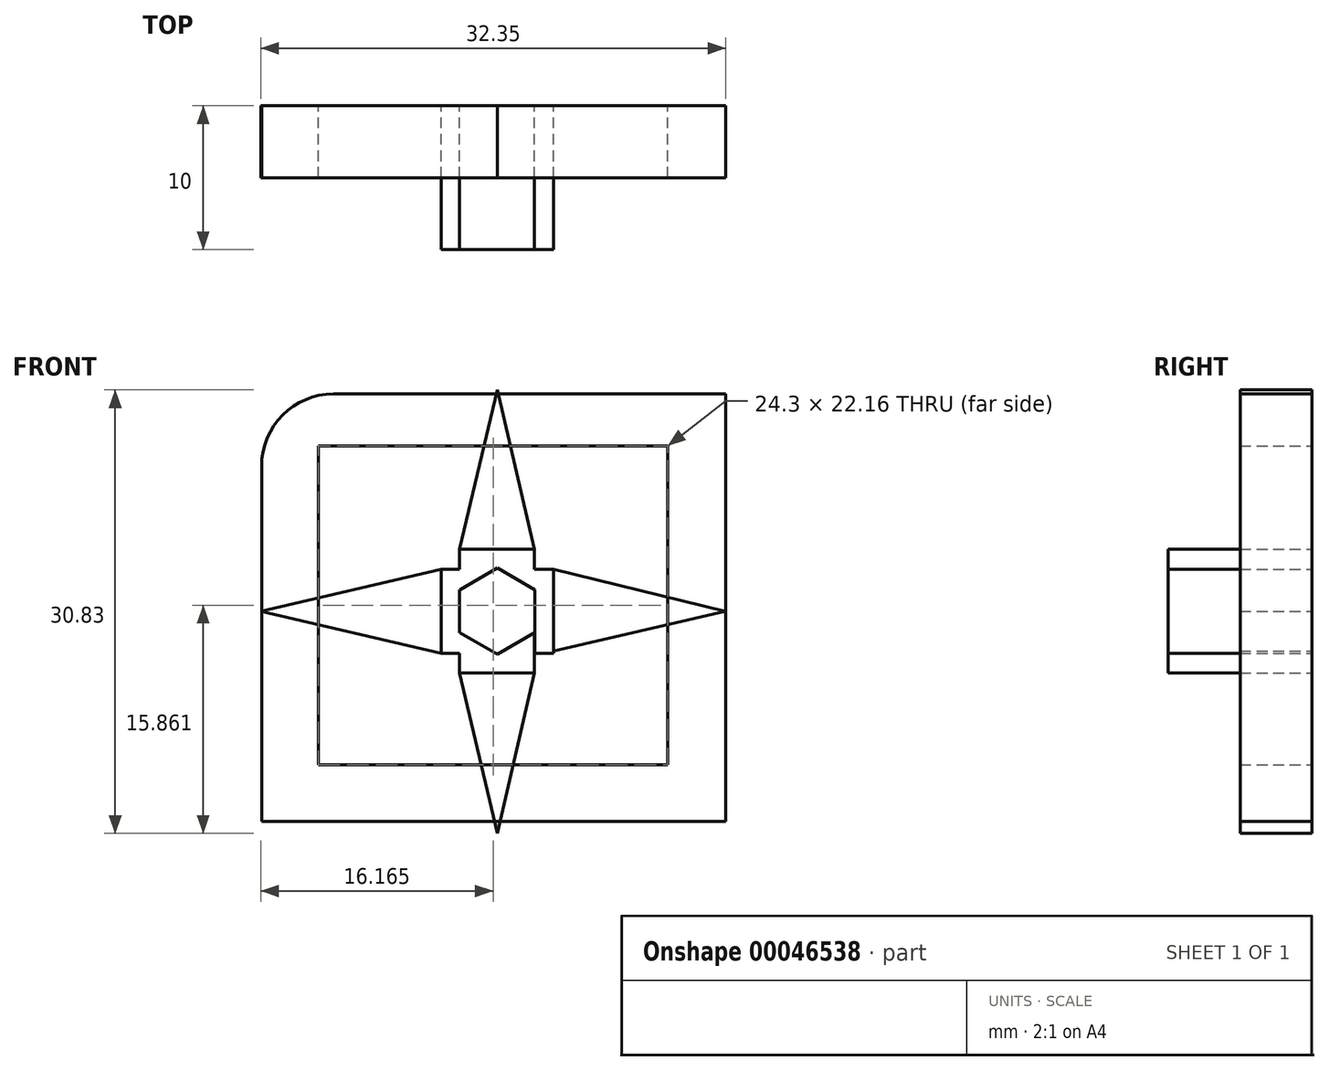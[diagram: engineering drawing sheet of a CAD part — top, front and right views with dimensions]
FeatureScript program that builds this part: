
annotation { "Feature Type Name" : "Feature", "Feature Type Description" : "" }
export const myFeature = defineFeature(function(context is Context, id is Id, definition is map)
    precondition{}
    {
        {
            var Q0;
            Q0=qCreatedBy(makeId("Front.planeOp"),FACE);
            var sketch = newSketch(context, id + "F0", { "sketchPlane" : qUnion([Q0])});
            skCircle(sketch, "E0.cCircle", {"center": v(0, 0) * mm, "radius": 2.6 * mm, "construction": true});
            skLineSegment(sketch, "E0.0", {"start": v(-2.6, -1.5) * mm, "end": v(-2.6, 1.5) * mm});
            skLineSegment(sketch, "E0.1", {"start": v(-2.6, 1.5) * mm, "end": v(0, 3) * mm});
            skLineSegment(sketch, "E0.2", {"start": v(0, 3) * mm, "end": v(2.6, 1.5) * mm});
            skLineSegment(sketch, "E0.3", {"start": v(2.6, 1.5) * mm, "end": v(2.6, -1.5) * mm});
            skLineSegment(sketch, "E0.4", {"start": v(2.6, -1.5) * mm, "end": v(0, -3) * mm});
            skLineSegment(sketch, "E0.5", {"start": v(0, -3) * mm, "end": v(-2.6, -1.5) * mm});
            skPoint(sketch, "E0.0.midPoint", {"position": v(-2.6, 0) * mm});
            skSolve(sketch);
        }
        {
            var Q0;
            Q0=makeQuery(id+"F0.imprint","IMPRINT",FACE,{"disambiguationData":[TD([[makeQuery(id+"F0.imprint","IMPRINT",EDGE,{"derivedFrom":sQuery(id+"F0.wireOp",EDGE,"E0.0")}),-1.0]])]});
            var sketch = newSketch(context, id + "F1", { "sketchPlane" : qUnion([Q0])});
            skLineSegment(sketch, "E1.bottom", {"start": v(-2.63, 1.5) * mm, "end": v(2.6, 1.5) * mm});
            skLineSegment(sketch, "E1.top", {"start": v(-2.63, 2.93) * mm, "end": v(2.6, 2.93) * mm});
            skLineSegment(sketch, "E1.left", {"start": v(-2.63, 1.5) * mm, "end": v(-2.63, 2.93) * mm});
            skLineSegment(sketch, "E1.right", {"start": v(2.6, 1.5) * mm, "end": v(2.6, 2.93) * mm});
            skLineSegment(sketch, "E2.bottom", {"start": v(-2.63, -1.48) * mm, "end": v(2.58, -1.48) * mm});
            skLineSegment(sketch, "E2.top", {"start": v(-2.63, -2.92) * mm, "end": v(2.58, -2.92) * mm});
            skLineSegment(sketch, "E2.left", {"start": v(-2.63, -1.48) * mm, "end": v(-2.63, -2.92) * mm});
            skLineSegment(sketch, "E2.right", {"start": v(2.58, -1.48) * mm, "end": v(2.58, -2.92) * mm});
            skLineSegment(sketch, "E3.bottom", {"start": v(-2.63, 2.93) * mm, "end": v(-3.9, 2.93) * mm});
            skLineSegment(sketch, "E3.top", {"start": v(-2.63, -2.92) * mm, "end": v(-3.9, -2.92) * mm});
            skLineSegment(sketch, "E3.left", {"start": v(-2.63, 2.93) * mm, "end": v(-2.63, -2.92) * mm});
            skLineSegment(sketch, "E3.right", {"start": v(-3.9, 2.93) * mm, "end": v(-3.9, -2.92) * mm});
            skLineSegment(sketch, "E4.bottom", {"start": v(2.6, 2.93) * mm, "end": v(3.9, 2.93) * mm});
            skLineSegment(sketch, "E4.top", {"start": v(2.6, -2.92) * mm, "end": v(3.9, -2.92) * mm});
            skLineSegment(sketch, "E4.left", {"start": v(2.6, 2.93) * mm, "end": v(2.6, -2.92) * mm});
            skLineSegment(sketch, "E4.right", {"start": v(3.9, 2.93) * mm, "end": v(3.9, -2.92) * mm});
            skLineSegment(sketch, "E5.bottom", {"start": v(-2.63, 2.93) * mm, "end": v(2.58, 2.93) * mm});
            skLineSegment(sketch, "E5.top", {"start": v(-2.63, 4.32) * mm, "end": v(2.58, 4.32) * mm});
            skLineSegment(sketch, "E5.left", {"start": v(-2.63, 2.93) * mm, "end": v(-2.63, 4.32) * mm});
            skLineSegment(sketch, "E5.right", {"start": v(2.58, 2.93) * mm, "end": v(2.58, 4.32) * mm});
            skLineSegment(sketch, "E6.top", {"start": v(-2.63, -4.28) * mm, "end": v(2.58, -4.28) * mm});
            skLineSegment(sketch, "E6.left", {"start": v(-2.63, -2.92) * mm, "end": v(-2.63, -4.28) * mm});
            skLineSegment(sketch, "E6.right", {"start": v(2.58, -2.92) * mm, "end": v(2.58, -4.28) * mm});
            skSolve(sketch);
        }
        {
            var Q0;
            {var subQ1=makeQuery(id+"F0.imprint","IMPRINT",EDGE,{"derivedFrom":sQuery(id+"F0.wireOp",EDGE,"E0.4")});var subQ3=sQuery(id+"F1.wireOp",EDGE,"E2.right");var subQ5=makeQuery(id+"F1.imprint","INTERSECT",VERTEX,{"derivedFrom":[subQ1,subQ3]});Q0=makeQuery(id+"F1.imprint","IMPRINT",FACE,{"disambiguationData":[TD([[makeQuery(id+"F1.imprint","IMPRINT",EDGE,{"disambiguationData":[TD([[subQ5,-1.0]])],"derivedFrom":subQ1}),1.0]])]});}
            var Q1;
            {var subQ0=sQuery(id+"F1.wireOp",EDGE,"E4.bottom");Q1=makeQuery(id+"F1.imprint","IMPRINT",FACE,{"disambiguationData":[TD([[makeQuery(id+"F1.imprint","IMPRINT",EDGE,{"derivedFrom":subQ0}),-1.0]])]});}
            var Q2;
            {var subQ9=sQuery(id+"F1.wireOp",EDGE,"E1.top");Q2=makeQuery(id+"F1.imprint","IMPRINT",FACE,{"disambiguationData":[TD([[makeQuery(id+"F1.imprint","IMPRINT",EDGE,{"derivedFrom":subQ9}),-1.0]])]});}
            var Q3;
            Q3=makeQuery(id+"F1.imprint","IMPRINT",FACE,{"disambiguationData":[TD([[makeQuery(id+"F1.imprint","IMPRINT",EDGE,{"derivedFrom":sQuery(id+"F1.wireOp",EDGE,"E5.top")}),-1.0]])]});
            var Q4;
            {var subQ5=sQuery(id+"F1.wireOp",EDGE,"E1.bottom");var subQ7=sQuery(id+"F1.wireOp",EDGE,"E3.left");var subQ8=makeQuery(id+"F1.imprint","INTERSECT",VERTEX,{"derivedFrom":[subQ5,subQ7]});Q4=makeQuery(id+"F1.imprint","IMPRINT",FACE,{"disambiguationData":[TD([[makeQuery(id+"F1.imprint","IMPRINT",EDGE,{"disambiguationData":[TD([[subQ8,-1.0]])],"derivedFrom":subQ5}),1.0]])]});}
            var Q5;
            {var subQ3=sQuery(id+"F1.wireOp",EDGE,"E3.bottom");Q5=makeQuery(id+"F1.imprint","IMPRINT",FACE,{"disambiguationData":[TD([[makeQuery(id+"F1.imprint","IMPRINT",EDGE,{"derivedFrom":subQ3}),1.0]])]});}
            var Q6;
            Q6=makeQuery(id+"F1.imprint","IMPRINT",FACE,{"disambiguationData":[TD([[makeQuery(id+"F1.imprint","IMPRINT",EDGE,{"derivedFrom":sQuery(id+"F1.wireOp",EDGE,"E6.top")}),1.0]])]});
            var Q7;
            {var subQ0=sQuery(id+"F1.wireOp",EDGE,"E2.bottom");var subQ3=sQuery(id+"F1.wireOp",EDGE,"E3.left");var subQ4=makeQuery(id+"F1.imprint","INTERSECT",VERTEX,{"derivedFrom":[subQ0,subQ3]});Q7=makeQuery(id+"F1.imprint","IMPRINT",FACE,{"disambiguationData":[TD([[makeQuery(id+"F1.imprint","IMPRINT",EDGE,{"disambiguationData":[TD([[subQ4,-1.0]])],"derivedFrom":subQ0}),-1.0]])]});}
            extrude(context, id + "F2", {"entities" : qUnion([Q0, Q1, Q2, Q3, Q4, Q5, Q6, Q7]), "depth" : 10 * mm});
        }
        {
            var Q0;
            Q0=makeQuery(id+"F2.opExtrude","CAP_FACE",FACE,{"disambiguationData":[OSD([sQuery(id+"F0.wireOp",EDGE,"E0.0"),sQuery(id+"F0.wireOp",EDGE,"E0.1"),sQuery(id+"F0.wireOp",EDGE,"E0.2"),sQuery(id+"F0.wireOp",EDGE,"E0.3"),sQuery(id+"F0.wireOp",EDGE,"E0.4"),sQuery(id+"F0.wireOp",EDGE,"E0.5"),sQuery(id+"F1.wireOp",EDGE,"E1.bottom"),sQuery(id+"F1.wireOp",EDGE,"E1.top"),sQuery(id+"F1.wireOp",EDGE,"E2.bottom"),sQuery(id+"F1.wireOp",EDGE,"E2.right"),sQuery(id+"F1.wireOp",EDGE,"E3.bottom"),sQuery(id+"F1.wireOp",EDGE,"E3.top"),sQuery(id+"F1.wireOp",EDGE,"E3.left"),sQuery(id+"F1.wireOp",EDGE,"E3.right"),sQuery(id+"F1.wireOp",EDGE,"E4.bottom"),sQuery(id+"F1.wireOp",EDGE,"E4.top"),sQuery(id+"F1.wireOp",EDGE,"E4.left"),sQuery(id+"F1.wireOp",EDGE,"E4.right"),sQuery(id+"F1.wireOp",EDGE,"E5.top"),sQuery(id+"F1.wireOp",EDGE,"E5.left"),sQuery(id+"F1.wireOp",EDGE,"E5.right"),sQuery(id+"F1.wireOp",EDGE,"E6.top"),sQuery(id+"F1.wireOp",EDGE,"E6.left"),sQuery(id+"F1.wireOp",EDGE,"E6.right")])],"isStart":true});
            var sketch = newSketch(context, id + "F3", { "sketchPlane" : qUnion([Q0])});
            skLineSegment(sketch, "E7", {"start": v(0, 3.05) * mm, "end": v(0, 15.38) * mm});
            skLineSegment(sketch, "E8", {"start": v(0, 15.38) * mm, "end": v(-2.58, 4.32) * mm});
            skLineSegment(sketch, "E9", {"start": v(0, 15.38) * mm, "end": v(2.63, 4.32) * mm});
            skLineSegment(sketch, "E10", {"start": v(-2.58, -4.28) * mm, "end": v(0, -15.45) * mm});
            skLineSegment(sketch, "E11", {"start": v(2.63, -4.28) * mm, "end": v(0, -15.45) * mm});
            skLineSegment(sketch, "E12", {"start": v(-3.9, 2.93) * mm, "end": v(-15.84, 0) * mm});
            skLineSegment(sketch, "E13", {"start": v(-15.84, 0) * mm, "end": v(-3.25, -2.92) * mm});
            skLineSegment(sketch, "E14", {"start": v(3.9, 2.93) * mm, "end": v(16.46, 0) * mm});
            skLineSegment(sketch, "E15", {"start": v(16.46, 0) * mm, "end": v(3.9, -2.92) * mm});
            skSolve(sketch);
        }
        {
            var Q0;
            {var subQ3=sQuery(id+"F3.wireOp",EDGE,"E12");Q0=makeQuery(id+"F3.imprint","IMPRINT",FACE,{"disambiguationData":[TD([[makeQuery(id+"F3.imprint","IMPRINT",EDGE,{"derivedFrom":subQ3}),1.0]])]});}
            var Q1;
            {var subQ0=sQuery(id+"F3.wireOp",EDGE,"E8");Q1=makeQuery(id+"F3.imprint","IMPRINT",FACE,{"disambiguationData":[TD([[makeQuery(id+"F3.imprint","IMPRINT",EDGE,{"derivedFrom":subQ0}),1.0]])]});}
            var Q2;
            {var subQ3=sQuery(id+"F3.wireOp",EDGE,"E9");Q2=makeQuery(id+"F3.imprint","IMPRINT",FACE,{"disambiguationData":[TD([[makeQuery(id+"F3.imprint","IMPRINT",EDGE,{"derivedFrom":subQ3}),-1.0]])]});}
            var Q3;
            Q3=makeQuery(id+"F3.imprint","IMPRINT",FACE,{"disambiguationData":[TD([[makeQuery(id+"F3.imprint","IMPRINT",EDGE,{"derivedFrom":sQuery(id+"F3.wireOp",EDGE,"E14")}),-1.0]])]});
            var Q4;
            Q4=makeQuery(id+"F3.imprint","IMPRINT",FACE,{"disambiguationData":[TD([[makeQuery(id+"F3.imprint","IMPRINT",EDGE,{"derivedFrom":sQuery(id+"F3.wireOp",EDGE,"E10")}),1.0]])]});
            extrude(context, id + "F4", {"entities" : qUnion([Q0, Q1, Q2, Q3, Q4]), "oppositeDirection" : true, "depth" : 5 * mm});
        }
        {
            var Q0;
            Q0=qCreatedBy(makeId("Front.planeOp"),FACE);
            var sketch = newSketch(context, id + "F5", { "sketchPlane" : qUnion([Q0])});
            skLineSegment(sketch, "E16.bottom", {"start": v(15.9, -10.67) * mm, "end": v(-16.4, -10.67) * mm});
            skLineSegment(sketch, "E16.top", {"start": v(15.9, -14.62) * mm, "end": v(-16.4, -14.62) * mm});
            skLineSegment(sketch, "E16.left", {"start": v(15.9, -10.67) * mm, "end": v(15.9, -14.62) * mm});
            skLineSegment(sketch, "E16.right", {"start": v(-16.4, -10.67) * mm, "end": v(-16.4, -14.62) * mm});
            skLineSegment(sketch, "E17.bottom", {"start": v(-16.4, -14.62) * mm, "end": v(-12.45, -14.62) * mm});
            skLineSegment(sketch, "E17.top", {"start": v(-16.4, 15.1) * mm, "end": v(-12.45, 15.1) * mm});
            skLineSegment(sketch, "E17.left", {"start": v(-16.4, -14.62) * mm, "end": v(-16.4, 15.1) * mm});
            skLineSegment(sketch, "E17.right", {"start": v(-12.45, -14.62) * mm, "end": v(-12.45, 15.1) * mm});
            skLineSegment(sketch, "E18.bottom", {"start": v(-12.45, 15.1) * mm, "end": v(15.9, 15.1) * mm});
            skLineSegment(sketch, "E18.top", {"start": v(-12.45, 11.49) * mm, "end": v(15.9, 11.49) * mm});
            skLineSegment(sketch, "E18.left", {"start": v(-12.45, 15.1) * mm, "end": v(-12.45, 11.49) * mm});
            skLineSegment(sketch, "E18.right", {"start": v(15.9, 15.1) * mm, "end": v(15.9, 11.49) * mm});
            skLineSegment(sketch, "E19.bottom", {"start": v(15.9, 15.1) * mm, "end": v(11.86, 15.1) * mm});
            skLineSegment(sketch, "E19.top", {"start": v(15.9, -14.62) * mm, "end": v(11.86, -14.62) * mm});
            skLineSegment(sketch, "E19.left", {"start": v(15.9, 15.1) * mm, "end": v(15.9, -14.62) * mm});
            skLineSegment(sketch, "E19.right", {"start": v(11.86, 15.1) * mm, "end": v(11.86, -14.62) * mm});
            skSolve(sketch);
        }
        {
            var Q0;
            {var subQ0=sQuery(id+"F5.wireOp",EDGE,"E19.left");var subQ3=sQuery(id+"F5.wireOp",EDGE,"E16.bottom");var subQ4=makeQuery(id+"F5.imprint","INTERSECT",VERTEX,{"derivedFrom":[subQ3,subQ0]});Q0=makeQuery(id+"F5.imprint","IMPRINT",FACE,{"disambiguationData":[TD([[makeQuery(id+"F5.imprint","IMPRINT",EDGE,{"disambiguationData":[TD([[subQ4,-1.0]])],"derivedFrom":subQ3}),-1.0]])]});}
            var Q1;
            {var subQ3=sQuery(id+"F5.wireOp",EDGE,"E18.bottom");Q1=makeQuery(id+"F5.imprint","IMPRINT",FACE,{"disambiguationData":[TD([[makeQuery(id+"F5.imprint","IMPRINT",EDGE,{"derivedFrom":subQ3}),-1.0]])]});}
            var Q2;
            {var subQ6=sQuery(id+"F5.wireOp",EDGE,"E17.top");Q2=makeQuery(id+"F5.imprint","IMPRINT",FACE,{"disambiguationData":[TD([[makeQuery(id+"F5.imprint","IMPRINT",EDGE,{"derivedFrom":subQ6}),-1.0]])]});}
            var Q3;
            {var subQ3=sQuery(id+"F5.wireOp",EDGE,"E17.bottom");Q3=makeQuery(id+"F5.imprint","IMPRINT",FACE,{"disambiguationData":[TD([[makeQuery(id+"F5.imprint","IMPRINT",EDGE,{"derivedFrom":subQ3}),1.0]])]});}
            var Q4;
            {var subQ3=sQuery(id+"F5.wireOp",EDGE,"E16.top");Q4=makeQuery(id+"F5.imprint","IMPRINT",FACE,{"disambiguationData":[TD([[makeQuery(id+"F5.imprint","IMPRINT",EDGE,{"derivedFrom":subQ3}),-1.0]])]});}
            var Q5;
            {var subQ3=sQuery(id+"F5.wireOp",EDGE,"E19.top");Q5=makeQuery(id+"F5.imprint","IMPRINT",FACE,{"disambiguationData":[TD([[makeQuery(id+"F5.imprint","IMPRINT",EDGE,{"derivedFrom":subQ3}),-1.0]])]});}
            var Q6;
            {var subQ3=sQuery(id+"F5.wireOp",EDGE,"E19.bottom");Q6=makeQuery(id+"F5.imprint","IMPRINT",FACE,{"disambiguationData":[TD([[makeQuery(id+"F5.imprint","IMPRINT",EDGE,{"derivedFrom":subQ3}),1.0]])]});}
            extrude(context, id + "F6", {"entities" : qUnion([Q0, Q1, Q2, Q3, Q4, Q5, Q6]), "depth" : 5 * mm});
        }
        {
            var Q0;
            Q0=makeQuery(id+"F6.opExtrude","SWEPT_EDGE",EDGE,{"disambiguationData":[OSD([sQuery(id+"F5.wireOp",EDGE,"E19.top"),sQuery(id+"F5.wireOp",EDGE,"E19.left")])]});
            var Q1;
            Q1=makeQuery(id+"F6.opExtrude","SWEPT_EDGE",EDGE,{"disambiguationData":[OSD([sQuery(id+"F5.wireOp",EDGE,"E17.bottom"),sQuery(id+"F5.wireOp",EDGE,"E17.left")])]});
            var Q2;
            Q2=makeQuery(id+"F6.opExtrude","SWEPT_EDGE",EDGE,{"disambiguationData":[OSD([sQuery(id+"F5.wireOp",EDGE,"E19.bottom"),sQuery(id+"F5.wireOp",EDGE,"E19.left")])]});
            var Q3;
            Q3=makeQuery(id+"F6.opExtrude","SWEPT_EDGE",EDGE,{"disambiguationData":[OSD([sQuery(id+"F5.wireOp",EDGE,"E17.top"),sQuery(id+"F5.wireOp",EDGE,"E17.left")])]});
            fillet(context, id + "F7", {"entities" : qUnion([Q0, Q1, Q2, Q3]), "radius" : 5 * mm, "tangentPropagation" : true, "allowEdgeOverflow" : false});
        }
    });
